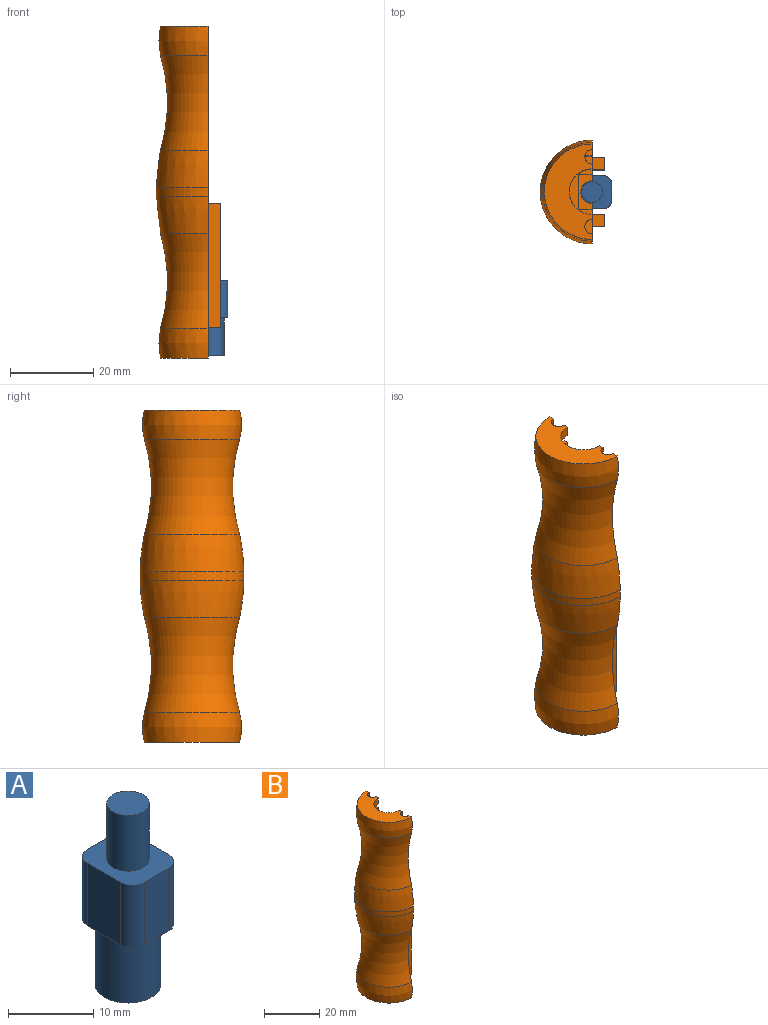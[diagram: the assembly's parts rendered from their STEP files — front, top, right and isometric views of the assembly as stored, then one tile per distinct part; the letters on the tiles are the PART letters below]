
ASSEMBLY  parts=2 mates=1
PART A: 14 faces, bbox 8x9.5x26 mm
  f0: plane 9x5.5mm, normal (-1,0,0), area 49.5mm2, adj f4,f5,f9,f12
  f1: plane 9x4mm, normal (0,-1,0), area 36mm2, adj f4,f5,f9,f10
  f2: plane 9x5.5mm, normal (1,0,0), area 49.5mm2, adj f4,f5,f10,f11
  f3: plane 9x4mm, normal (0,1,0), area 36mm2, adj f4,f5,f11,f12
  f4: plane 9.5x8mm, normal (0,0,1), area 52.9mm2, adj f0,f1,f2,f3,f7,f9,f10,f11
  f5: plane 9.5x8mm, normal (0,0,-1), area 25.4mm2, adj f0,f1,f2,f3,f6,f9,f10,f11
  f6: cylinder r=3.88mm len=9mm, axis (0,0,-1), area 219.1mm2, adj f5,f13
  f7: cylinder r=2.5mm len=8mm, axis (0,0,-1), area 125.7mm2, adj f4,f8
  f8: plane 5x5mm, normal (0,0,1), area 19.6mm2, adj f7
  f9: cylinder r=2mm len=9mm, axis (0,0,1), area 28.3mm2, adj f0,f1,f4,f5
  f10: cylinder r=2mm len=9mm, axis (0,0,-1), area 28.3mm2, adj f1,f2,f4,f5
  f11: cylinder r=2mm len=9mm, axis (0,0,1), area 28.3mm2, adj f2,f3,f4,f5
  f12: cylinder r=2mm len=9mm, axis (0,0,-1), area 28.3mm2, adj f0,f3,f4,f5
  f13: plane 7.75x7.75mm, normal (0,0,-1), area 47.2mm2, adj f6
PART B: 60 faces, bbox 26.2x46.4x99.8 mm
  f0: plane 80x9.75mm, normal (1,0,0), area 266.5mm2, adj f1,f8,f9,f11,f12,f13,f14,f15
  f1: plane 23x11.5mm, normal (0,0,-1), area 179.4mm2, adj f0,f7,f15,f55
  f2: cylinder r=5.5mm len=25.5mm, axis (0,0,-1), area 392.2mm2, adj f3,f6,f7,f21,f33,f35,f51,f53
  f3: plane 19.86x10.16mm, normal (0,0,1), area 101mm2, adj f2,f6,f7,f8,f26,f51,f52,f53
  f4: plane 2.5x1.16mm, normal (1,0,0), area 2.9mm2, adj f5,f10,f12,f29
  f5: cylinder r=5.5mm len=11mm, axis (0,0,-1), area 43.2mm2, adj f4,f12,f29,f32
  f6: plane 27.5x2.41mm, normal (1,0,0), area 34.3mm2, adj f2,f3,f9,f21,f26,f27
  f7: plane 80x9.75mm, normal (1,0,0), area 353.4mm2, adj f1,f2,f3,f8,f10,f12,f13,f14
  f8: cylinder r=10.16mm len=20.31mm, axis (0,0,1), area 61.8mm2, adj f0,f3,f7,f29,f31,f57,f58
  f9: plane 30x3.25mm, normal (0,-1,0), area 67.5mm2, adj f0,f6,f21,f22,f27,f28,f30,f59
  f10: cylinder r=1.75mm len=3.5mm, axis (0,0,1), area 13.7mm2, adj f4,f7,f12,f29
  f11: cylinder r=1.75mm len=3.5mm, axis (0,0,1), area 13.7mm2, adj f0,f12,f29,f32
  f12: plane 23x11.5mm, normal (0,0,1), area 150.6mm2, adj f0,f4,f5,f7,f10,f11,f18,f32
  f13: torus R=49.81mm, axis (0,0,1), area 760.4mm2, adj f0,f7,f14,f15
  f14: revolved ~25x12.5mm, area 345.3mm2, adj f0,f7,f13,f19
  f15: revolved ~23.83x11.91mm, area 261.4mm2, adj f0,f1,f7,f13
  f16: revolved ~25x12.5mm, area 345.3mm2, adj f0,f7,f17,f19
  f17: torus R=49.81mm, axis (0,0,1), area 760.4mm2, adj f0,f7,f16,f18
  f18: revolved ~23.83x11.91mm, area 261.4mm2, adj f0,f7,f12,f17
  f19: cylinder r=12.5mm len=25mm, axis (0,0,-1), area 79.3mm2, adj f0,f7,f14,f16
  f20: plane 30x3.25mm, normal (0,1,0), area 97.5mm2, adj f7,f21,f22,f30
  f21: plane 14x5.5mm, normal (0,0,1), area 26.1mm2, adj f2,f6,f7,f9,f20,f30,f34,f35
  f22: plane 8.5x3.25mm, normal (0,0,1), area 15.7mm2, adj f0,f7,f9,f20,f30,f56
  f23: plane 37.47x3mm, normal (0,-1,0), area 112.4mm2, adj f0,f24,f28,f59
  f24: plane 3x1.5mm, normal (0,0,1), area 4.5mm2, adj f0,f23,f25,f59
  f25: plane 3x2mm, normal (0,-1,0), area 6mm2, adj f0,f24,f31,f59
  f26: plane 27.5x3mm, normal (0,1,0), area 82.5mm2, adj f3,f6,f27,f59
  f27: plane 3x2.41mm, normal (0,0,-1), area 7.2mm2, adj f6,f9,f26,f59
  f28: plane 4.41x3mm, normal (0,0,1), area 13.2mm2, adj f0,f9,f23,f59
  f29: plane 20.31x10.16mm, normal (0,0,-1), area 104.9mm2, adj f4,f5,f8,f10,f11,f32
  f30: plane 30x8.5mm, normal (1,0,0), area 255mm2, adj f9,f20,f21,f22
  f31: plane 3x0.05mm, normal (0,0,-1), area 0.1mm2, adj f8,f25,f58,f59
  f32: plane 2.5x1.16mm, normal (1,0,0), area 2.9mm2, adj f5,f11,f12,f29
  f33: plane 3.38x2mm, normal (0,0,-1), area 6.2mm2, adj f2,f7,f34,f35
  f34: plane 15.5x2mm, normal (0,1,0), area 31mm2, adj f7,f21,f33,f35
  f35: plane 15.5x3.38mm, normal (1,0,0), area 52.3mm2, adj f2,f21,f33,f34
  f36: plane 8.5x5mm, normal (0,0,1), area 14.1mm2, adj f37,f39,f40,f55
  f37: plane 14.96x5mm, normal (0,-1,0), area 74.8mm2, adj f0,f36,f38,f40
  f38: plane 8.5x5mm, normal (0,0,-1), area 30.6mm2, adj f0,f7,f37,f39,f40,f56
  f39: plane 14.96x5mm, normal (0,1,0), area 74.8mm2, adj f7,f36,f38,f40
  f40: plane 14.96x8.5mm, normal (1,0,0), area 127.2mm2, adj f36,f37,f38,f39
  f41: plane 30x3mm, normal (0,-1,0), area 90mm2, adj f7,f42,f44,f45
  f42: plane 3x3mm, normal (0,0,-1), area 9mm2, adj f7,f41,f43,f45
  f43: plane 30x3mm, normal (0,1,0), area 90mm2, adj f7,f42,f44,f45
  f44: plane 3x3mm, normal (0,0,1), area 9mm2, adj f7,f41,f43,f45
  f45: plane 30x3mm, normal (1,0,0), area 90mm2, adj f41,f42,f43,f44
  f46: plane 30x3mm, normal (0,1,0), area 90mm2, adj f0,f47,f49,f50
  f47: plane 3x3mm, normal (0,0,1), area 9mm2, adj f0,f46,f48,f50
  f48: plane 30x3mm, normal (0,-1,0), area 90mm2, adj f0,f47,f49,f50
  f49: plane 3x3mm, normal (0,0,-1), area 9mm2, adj f0,f46,f48,f50
  f50: plane 30x3mm, normal (1,0,0), area 90mm2, adj f46,f47,f48,f49
  f51: plane 5.5x1.19mm, normal (0,-1,0), area 6.6mm2, adj f2,f3,f52,f54
  f52: cylinder r=6.66mm len=5.5mm, axis (0,0,1), area 16.6mm2, adj f3,f51,f53,f54
  f53: plane 5.5x1.19mm, normal (0,1,0), area 6.6mm2, adj f2,f3,f52,f54
  f54: plane 3x1.37mm, normal (0,0,1), area 3.5mm2, adj f2,f51,f52,f53
  f55: cylinder r=4.25mm len=8.5mm, axis (0,0,-1), area 40.1mm2, adj f0,f1,f7,f36
  f56: cylinder r=2.75mm len=5.5mm, axis (0,0,1), area 17.6mm2, adj f0,f7,f22,f38
  f57: plane 2x0.4mm, normal (0,0,-1), area 0.3mm2, adj f8,f58,f59
  f58: plane 2x1.97mm, normal (0,1,0), area 3.9mm2, adj f8,f31,f57,f59
  f59: plane 39.47x5.91mm, normal (1,0,0), area 99.2mm2, adj f3,f9,f23,f24,f25,f26,f27,f28
PLACE A rot(axis=(0,0,-1),90deg) t=(56.68,55.82,24.96)mm
PLACE B t=(56.68,55.82,23.31)mm fixed
MATE slider B.f13 <-> A.f6  axis (0,0,-1) through (56.68,55.82,23.31)mm
